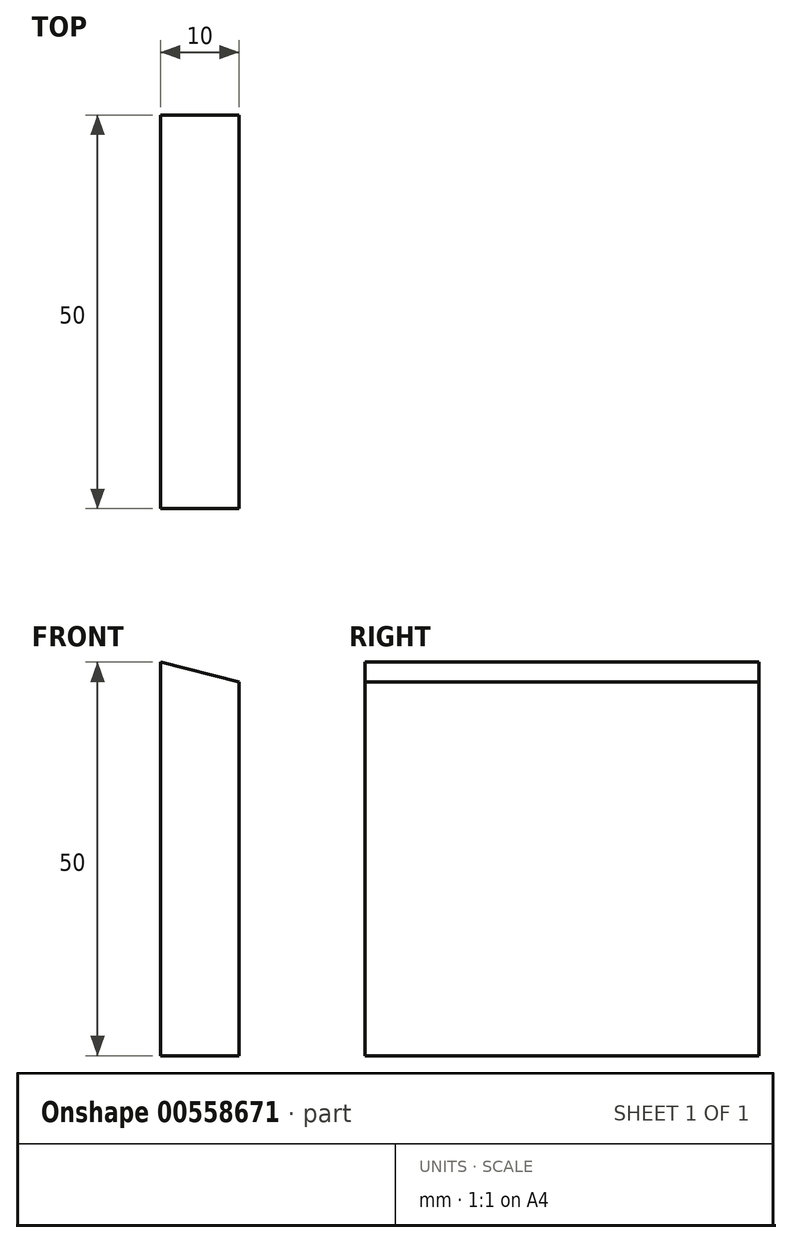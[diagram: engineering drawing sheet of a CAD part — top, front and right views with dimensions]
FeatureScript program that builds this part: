
annotation { "Feature Type Name" : "Feature", "Feature Type Description" : "" }
export const myFeature = defineFeature(function(context is Context, id is Id, definition is map)
    precondition{}
    {
        {
            var Q0;
            Q0=qCreatedBy(makeId("Front.planeOp"),FACE);
            var sketch = newSketch(context, id + "F0", { "sketchPlane" : qUnion([Q0])});
            skLineSegment(sketch, "E0", {"start": v(0, 0) * mm, "end": v(0, 50) * mm});
            skLineSegment(sketch, "E1", {"start": v(0, 50) * mm, "end": v(10, 47.5) * mm});
            skLineSegment(sketch, "E2", {"start": v(10, 47.5) * mm, "end": v(10, 0) * mm});
            skLineSegment(sketch, "E3", {"start": v(10, 0) * mm, "end": v(0, 0) * mm});
            skSolve(sketch);
        }
        {
            var Q0;
            Q0 = qSketchRegion(id + "F0", true);
            extrude(context, id + "F1", {"entities" : qUnion([Q0]), "depth" : 50 * mm, "offsetDistance" : 25 * mm});
        }
    });
